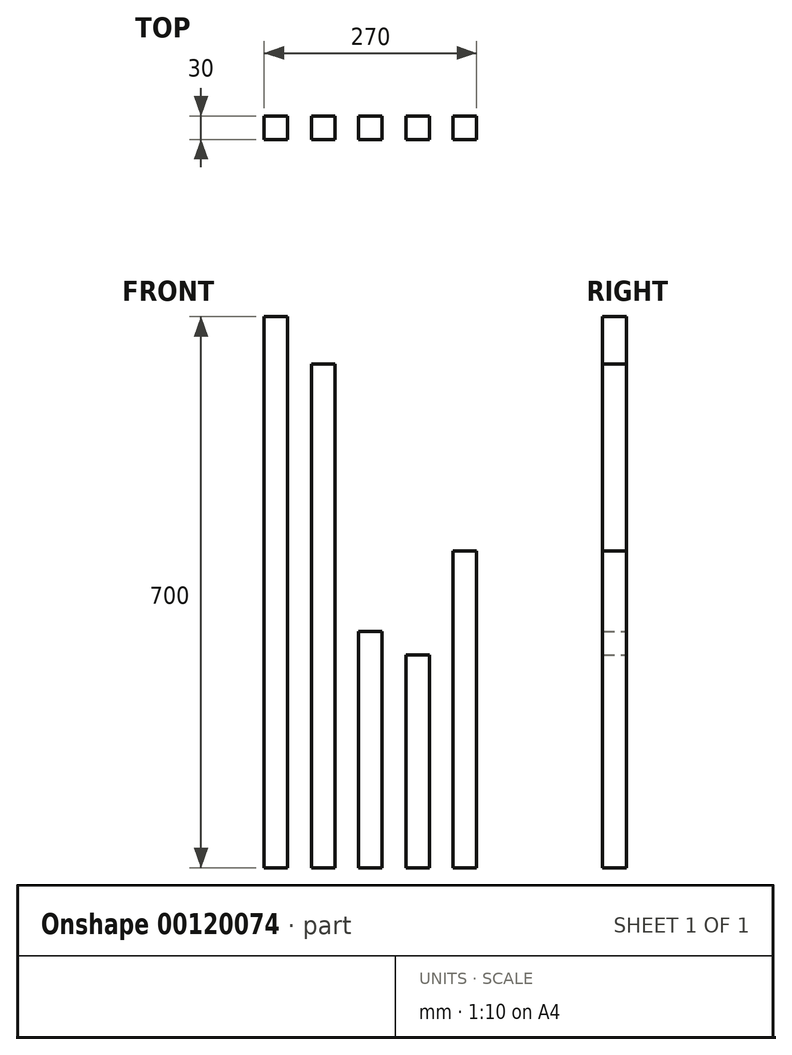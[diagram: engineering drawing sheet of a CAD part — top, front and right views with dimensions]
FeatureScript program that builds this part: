
annotation { "Feature Type Name" : "Feature", "Feature Type Description" : "" }
export const myFeature = defineFeature(function(context is Context, id is Id, definition is map)
    precondition{}
    {
        {
            var Q0;
            Q0=qCreatedBy(makeId("Front.planeOp"),FACE);
            var sketch = newSketch(context, id + "F0", { "sketchPlane" : qUnion([Q0])});
            skLineSegment(sketch, "E0.bottom", {"start": v(-60, 0) * mm, "end": v(-30, 0) * mm});
            skLineSegment(sketch, "E0.top", {"start": v(-60, 700) * mm, "end": v(-30, 700) * mm});
            skLineSegment(sketch, "E0.left", {"start": v(-60, 0) * mm, "end": v(-60, 700) * mm});
            skLineSegment(sketch, "E0.right", {"start": v(-30, 0) * mm, "end": v(-30, 700) * mm});
            skLineSegment(sketch, "E1.bottom", {"start": v(0, 0) * mm, "end": v(30, 0) * mm});
            skLineSegment(sketch, "E1.top", {"start": v(0, 640) * mm, "end": v(30, 640) * mm});
            skLineSegment(sketch, "E1.left", {"start": v(0, 0) * mm, "end": v(0, 640) * mm});
            skLineSegment(sketch, "E1.right", {"start": v(30, 0) * mm, "end": v(30, 640) * mm});
            skLineSegment(sketch, "E2.bottom", {"start": v(60, 0) * mm, "end": v(90, 0) * mm});
            skLineSegment(sketch, "E2.top", {"start": v(60, 300) * mm, "end": v(90, 300) * mm});
            skLineSegment(sketch, "E2.left", {"start": v(60, 0) * mm, "end": v(60, 300) * mm});
            skLineSegment(sketch, "E2.right", {"start": v(90, 0) * mm, "end": v(90, 300) * mm});
            skLineSegment(sketch, "E3.bottom", {"start": v(120, 0) * mm, "end": v(150, 0) * mm});
            skLineSegment(sketch, "E3.top", {"start": v(120, 270) * mm, "end": v(150, 270) * mm});
            skLineSegment(sketch, "E3.left", {"start": v(120, 0) * mm, "end": v(120, 270) * mm});
            skLineSegment(sketch, "E3.right", {"start": v(150, 0) * mm, "end": v(150, 270) * mm});
            skLineSegment(sketch, "E4.bottom", {"start": v(180, 0) * mm, "end": v(210, 0) * mm});
            skLineSegment(sketch, "E4.top", {"start": v(180, 402.5) * mm, "end": v(210, 402.5) * mm});
            skLineSegment(sketch, "E4.left", {"start": v(180, 0) * mm, "end": v(180, 402.5) * mm});
            skLineSegment(sketch, "E4.right", {"start": v(210, 0) * mm, "end": v(210, 402.5) * mm});
            skSolve(sketch);
        }
        {
            var Q0;
            Q0=makeQuery(id+"F0.imprint","IMPRINT",FACE,{"disambiguationData":[TD([[makeQuery(id+"F0.imprint","IMPRINT",EDGE,{"derivedFrom":sQuery(id+"F0.wireOp",EDGE,"E0.bottom")}),1.0]])]});
            var Q1;
            Q1=makeQuery(id+"F0.imprint","IMPRINT",FACE,{"disambiguationData":[TD([[makeQuery(id+"F0.imprint","IMPRINT",EDGE,{"derivedFrom":sQuery(id+"F0.wireOp",EDGE,"E1.bottom")}),1.0]])]});
            var Q2;
            Q2=makeQuery(id+"F0.imprint","IMPRINT",FACE,{"disambiguationData":[TD([[makeQuery(id+"F0.imprint","IMPRINT",EDGE,{"derivedFrom":sQuery(id+"F0.wireOp",EDGE,"E2.bottom")}),1.0]])]});
            var Q3;
            Q3=makeQuery(id+"F0.imprint","IMPRINT",FACE,{"disambiguationData":[TD([[makeQuery(id+"F0.imprint","IMPRINT",EDGE,{"derivedFrom":sQuery(id+"F0.wireOp",EDGE,"E3.bottom")}),1.0]])]});
            var Q4;
            Q4=makeQuery(id+"F0.imprint","IMPRINT",FACE,{"disambiguationData":[TD([[makeQuery(id+"F0.imprint","IMPRINT",EDGE,{"derivedFrom":sQuery(id+"F0.wireOp",EDGE,"E4.bottom")}),1.0]])]});
            extrude(context, id + "F1", {"entities" : qUnion([Q0, Q1, Q2, Q3, Q4]), "depth" : 30 * mm});
        }
    });
